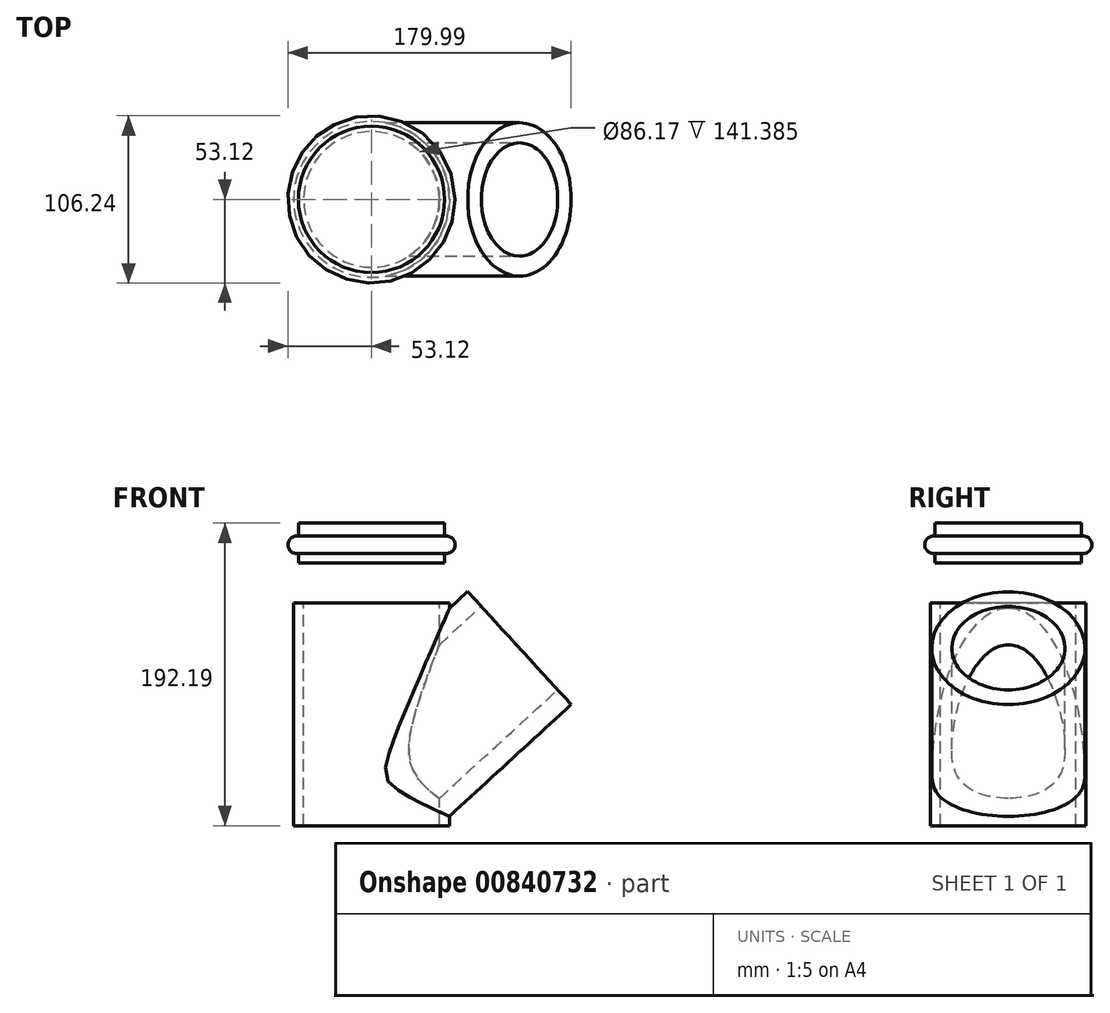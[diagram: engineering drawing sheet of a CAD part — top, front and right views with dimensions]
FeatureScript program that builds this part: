
annotation { "Feature Type Name" : "Feature", "Feature Type Description" : "" }
export const myFeature = defineFeature(function(context is Context, id is Id, definition is map)
    precondition{}
    {
        {
            var Q0;
            Q0=qCreatedBy(makeId("Top.planeOp"),FACE);
            var sketch = newSketch(context, id + "F0", { "sketchPlane" : qUnion([Q0])});
            skCircle(sketch, "E0", {"center": v(0, 0) * mm, "radius": 49.44 * mm});
            skSolve(sketch);
        }
        {
            var Q0;
            Q0=makeQuery(id+"F0.imprint","IMPRINT",FACE,{"disambiguationData":[TD([[makeQuery(id+"F0.imprint","IMPRINT",EDGE,{"derivedFrom":sQuery(id+"F0.wireOp",EDGE,"E0")}),1.0]])]});
            extrude(context, id + "F1", {"entities" : qUnion([Q0]), "depth" : 141.39 * mm, "offsetDistance" : 25.4 * mm});
        }
        {
            var Q0;
            Q0=makeQuery(id+"F1.opExtrude","CAP_FACE",FACE,{"disambiguationData":[OSD([sQuery(id+"F0.wireOp",EDGE,"E0")])],"isStart":false});
            var sketch = newSketch(context, id + "F2", { "sketchPlane" : qUnion([Q0])});
            skCircle(sketch, "E1.0", {"center": v(0, 0) * mm, "radius": 43.09 * mm});
            skSolve(sketch);
        }
        {
            var Q0;
            Q0=makeQuery(id+"F2.imprint","IMPRINT",FACE,{"disambiguationData":[TD([[makeQuery(id+"F2.imprint","IMPRINT",EDGE,{"derivedFrom":sQuery(id+"F2.wireOp",EDGE,"E1.0")}),1.0]])]});
            extrude(context, id + "F3", {"entities" : qUnion([Q0]), "operationType" : NewBodyOperationType.REMOVE, "oppositeDirection" : true, "depth" : 207.29 * mm, "offsetDistance" : 25.4 * mm});
        }
        {
            var Q0;
            Q0=qCreatedBy(makeId("Front.planeOp"),FACE);
            var sketch = newSketch(context, id + "F4", { "sketchPlane" : qUnion([Q0])});
            skLineSegment(sketch, "E2", {"start": v(22, 46.81) * mm, "end": v(93.99, 112.84) * mm});
            skSolve(sketch);
        }
        {
            var Q0;
            Q0=sQuery(id+"F4.wireOp",VERTEX,"E2.end");
            var Q1;
            Q1=sQuery(id+"F4.wireOp",EDGE,"E2");
            cPlane(context, id + "F5", {"entities" : qUnion([Q0, Q1]), "cplaneType" : CPlaneType.CURVE_POINT, "offset" : 25.4 * mm, "width" : 152.4 * mm, "height" : 152.4 * mm});
        }
        {
            var Q0;
            Q0=qCreatedBy(id+"F5.planeOp",FACE);
            var sketch = newSketch(context, id + "F6", { "sketchPlane" : qUnion([Q0])});
            skCircle(sketch, "E3", {"center": v(0, 19.62) * mm, "radius": 48.65 * mm});
            skCircle(sketch, "E4.0", {"center": v(0, 19.62) * mm, "radius": 35.95 * mm});
            skSolve(sketch);
        }
        {
            var Q0;
            Q0=makeQuery(id+"F6.imprint","IMPRINT",FACE,{"disambiguationData":[TD([[makeQuery(id+"F6.imprint","IMPRINT",EDGE,{"derivedFrom":sQuery(id+"F6.wireOp",EDGE,"E3")}),1.0]])]});
            var sketch = newSketch(context, id + "F7", { "sketchPlane" : qUnion([Q0])});
            skSolve(sketch);
        }
        {
            var Q0;
            Q0=makeQuery(id+"F7.imprint","IMPRINT",FACE,{"disambiguationData":[TD([[makeQuery(id+"F7.imprint","IMPRINT",EDGE,{"derivedFrom":makeQuery(id+"F6.imprint","IMPRINT",EDGE,{"derivedFrom":sQuery(id+"F6.wireOp",EDGE,"E3")})}),1.0]])]});
            extrude(context, id + "F8", {"entities" : qUnion([Q0]), "operationType" : NewBodyOperationType.ADD, "endBound" : BoundingType.UP_TO_NEXT, "oppositeDirection" : true, "depth" : 25.4 * mm, "offsetDistance" : 25.4 * mm});
        }
        {
            var Q0;
            Q0=makeQuery(id+"F6.imprint","IMPRINT",FACE,{"disambiguationData":[TD([[makeQuery(id+"F6.imprint","IMPRINT",EDGE,{"derivedFrom":sQuery(id+"F6.wireOp",EDGE,"E4.0")}),1.0]])]});
            var Q1;
            Q1=makeQuery(id+"F3.boolean.opBoolean","COPY",FACE,{"derivedFrom":makeQuery(id+"F3.opExtrude","SWEPT_FACE",FACE,{"disambiguationData":[OSD([sQuery(id+"F2.wireOp",EDGE,"E1.0")])]})});
            extrude(context, id + "F9", {"entities" : qUnion([Q0]), "operationType" : NewBodyOperationType.REMOVE, "endBound" : BoundingType.UP_TO_SURFACE, "oppositeDirection" : true, "depth" : 75.62 * mm, "endBoundEntityFace" : qUnion([Q1]), "offsetDistance" : 25.4 * mm});
        }
        {
            var Q0;
            Q0=makeQuery(id+"F1.opExtrude","CAP_FACE",FACE,{"disambiguationData":[OSD([sQuery(id+"F0.wireOp",EDGE,"E0")])],"isStart":false});
            cPlane(context, id + "F10", {"entities" : qUnion([Q0]), "cplaneType" : CPlaneType.OFFSET, "offset" : 25.4 * mm, "width" : 152.4 * mm, "height" : 152.4 * mm});
        }
        {
            var Q0;
            Q0=qCreatedBy(id+"F10.planeOp",FACE);
            var sketch = newSketch(context, id + "F11", { "sketchPlane" : qUnion([Q0])});
            skCircle(sketch, "E5", {"center": v(0, 0) * mm, "radius": 46.45 * mm});
            skSolve(sketch);
        }
        {
            var Q0;
            Q0=makeQuery(id+"F11.imprint","IMPRINT",FACE,{"disambiguationData":[TD([[makeQuery(id+"F11.imprint","IMPRINT",EDGE,{"derivedFrom":sQuery(id+"F11.wireOp",EDGE,"E5")}),1.0]])]});
            extrude(context, id + "F12", {"entities" : qUnion([Q0]), "depth" : 25.4 * mm, "offsetDistance" : 25.4 * mm});
        }
        {
            var Q0;
            Q0=qCreatedBy(makeId("Front.planeOp"),FACE);
            var sketch = newSketch(context, id + "F13", { "sketchPlane" : qUnion([Q0])});
            skCircle(sketch, "E6", {"center": v(47.58, 178.45) * mm, "radius": 5.54 * mm});
            skSolve(sketch);
        }
        {
            var Q0;
            Q0=makeQuery(id+"F13.imprint","IMPRINT",FACE,{"disambiguationData":[TD([[makeQuery(id+"F13.imprint","IMPRINT",EDGE,{"derivedFrom":sQuery(id+"F13.wireOp",EDGE,"E6")}),1.0]])]});
            var Q1;
            Q1=makeQuery(id+"F12.opExtrude","SWEPT_FACE",FACE,{"disambiguationData":[OSD([sQuery(id+"F11.wireOp",EDGE,"E5")])]});
            revolve(context, id + "F14", {"operationType" : NewBodyOperationType.ADD, "surfaceOperationType" : NewSurfaceOperationType.NEW, "entities" : qUnion([Q0]), "axis" : qUnion([Q1]), "revolveType" : RevolveType.FULL});
        }
    });
